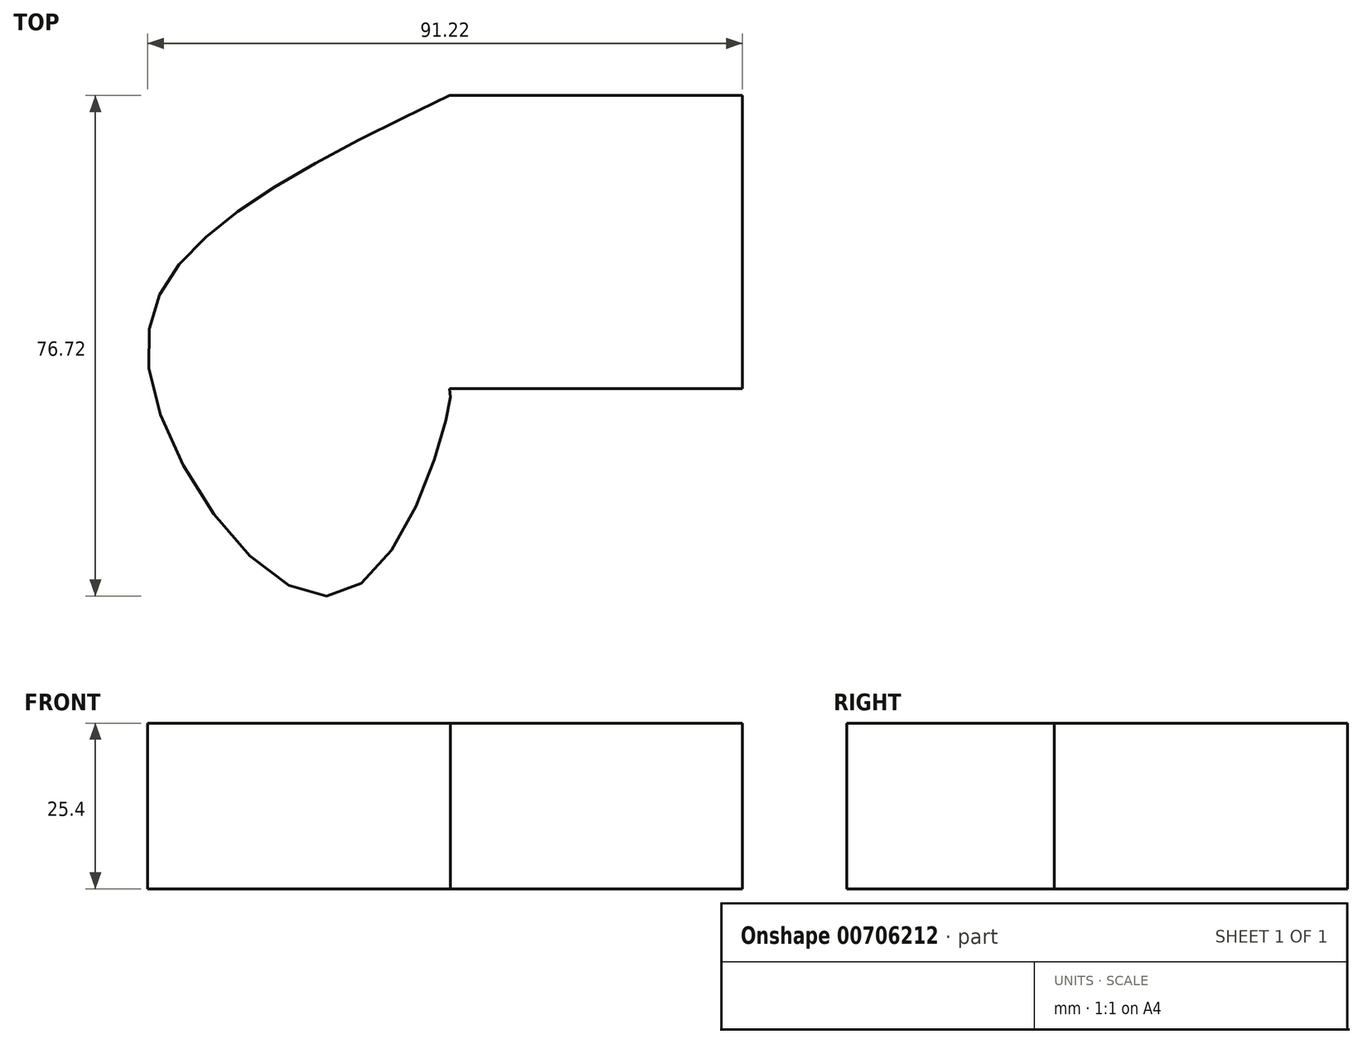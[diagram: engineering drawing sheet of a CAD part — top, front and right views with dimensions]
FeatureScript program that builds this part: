
annotation { "Feature Type Name" : "Feature", "Feature Type Description" : "" }
export const myFeature = defineFeature(function(context is Context, id is Id, definition is map)
    precondition{}
    {
        {
            var Q0;
            Q0=qCreatedBy(makeId("Top.planeOp"),FACE);
            var sketch = newSketch(context, id + "F0", { "sketchPlane" : qUnion([Q0])});
            skLineSegment(sketch, "E0.bottom", {"start": v(0, 0) * mm, "end": v(44.93, 0) * mm});
            skLineSegment(sketch, "E0.top", {"start": v(0, 44.93) * mm, "end": v(44.93, 44.93) * mm});
            skLineSegment(sketch, "E0.right", {"start": v(44.93, 0) * mm, "end": v(44.93, 44.93) * mm});
            skFitSpline(sketch, "E1", {"points": [v(0, 44.93) * mm, v(-36.98, 23.56) * mm, v(-45.52, 0) * mm, v(-16.8, -31.52) * mm, v(0, -2.31) * mm, v(0, 0) * mm], "startDerivative": vector(-162.52, -78.25) * mm, "endDerivative": vector(-6.2, 21) * mm});
            skSolve(sketch);
        }
        {
            var Q0;
            Q0 = qSketchRegion(id + "F0", true);
            extrude(context, id + "F1", {"entities" : qUnion([Q0]), "depth" : 25.4 * mm, "offsetDistance" : 25.4 * mm});
        }
    });
